# Revit family: DTT36M974_Revit
name_source: partatom
category: Specialty Equipment
revit_build: Autodesk Revit MEP 2014 (Build: 20130308_1515(x64)
units: mm (PartAtom-declared; Revit-internal decimal feet)

## types (1)
- DTT36M974
    Adjustment = Stainless Steel
    BLUETOOTH CONNECT BUTTON = YES
    BLUETOOTH CONNECT LED = YES
    Burner Support = Plastic-Black
    CIRCUIT BREAKER (A) = 15
    Depth = 24"
    Description = 36-INCH GAS RANGETOP MODERNIST COLLECTION
    ELECTRIC = 1,400W
    ENERGY SOURCE = GAS AND ELECTRIC
    FREQUENCY (HZ) = 60
    GAS TYPE = NATURAL GAS/LIQUID PROPANE
    Gas = Stainless Steel
    HIGH ALTITUDE AVAILABLE = YES
    Handle = Stainless Steel
    Height = 8"
    LED AMBIENT LIGHTING = YES
    LED CONTROL BUTTON = YES
    LED KNOB BACKLIGHTING = YES
    LEFT FRONT (BTU) = 18,000 DUAL (SIMMER)
    LEFT REAR (BTU) = 16,000 DUAL (SIMMER)
    LIMITED, PARTS AND LABOR = 1 YEAR
    Manufacturer = Dacor
    Model = DTT36M974
    OIL PAN = YES
    POWER CORD = YES
    RE-IGNITION = YES
    RIGHT FRONT (BTU) = 22,000 DUAL (SIMMER)
    RIGHT REAR (BTU) = 9,000 STACK DUAL (SIMMER)
    SEALED BURNERS = YES
    TOTAL NUMBER OF COOKTOP BURNERS = 4 (BRASS)
    Unit = Stainless Steel
    VOLTS (V) = 120
    WI FI CONNECT BUTTON = YES
    WI FI CONNECT LED = YES
    Width = 36"

## geometry (parser evidence)
native form markers: Sweep x1
no freeform markers — native parametric forms only
